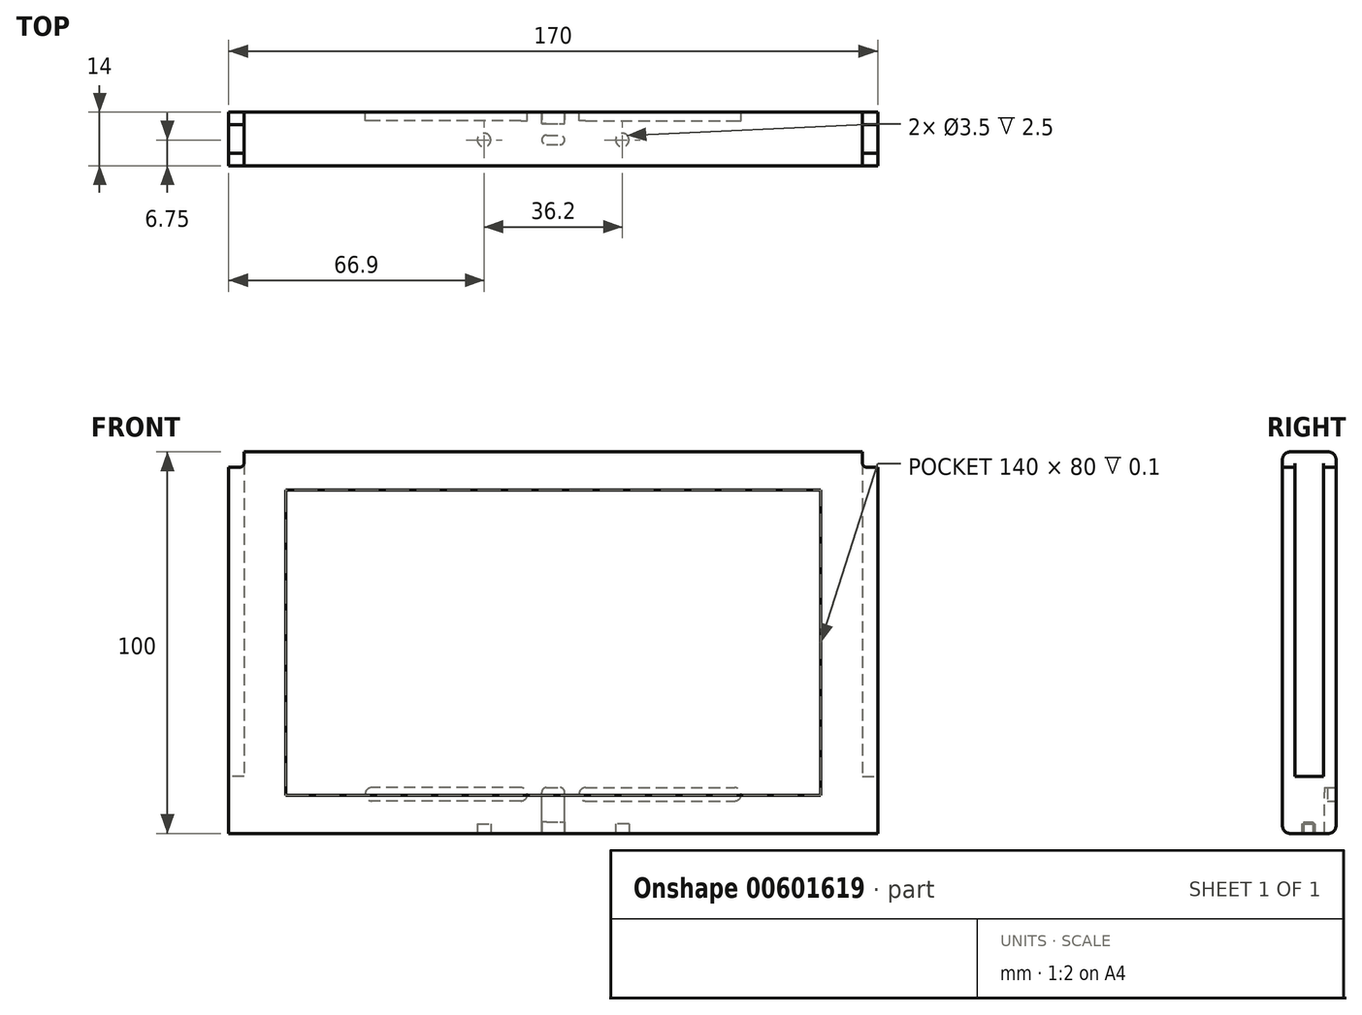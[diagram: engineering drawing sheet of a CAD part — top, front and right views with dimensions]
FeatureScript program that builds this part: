
annotation { "Feature Type Name" : "Feature", "Feature Type Description" : "" }
export const myFeature = defineFeature(function(context is Context, id is Id, definition is map)
    precondition{}
    {
        {
            var Q0;
            Q0=qCreatedBy(makeId("Front.planeOp"),FACE);
            var sketch = newSketch(context, id + "F0", { "sketchPlane" : qUnion([Q0])});
            skLineSegment(sketch, "E0.left", {"start": v(0, 0) * mm, "end": v(0, 100) * mm});
            skLineSegment(sketch, "E1", {"start": v(85, 100) * mm, "end": v(85, 0) * mm});
            skLineSegment(sketch, "E2", {"start": v(0, 0) * mm, "end": v(85, 0) * mm});
            skLineSegment(sketch, "E3", {"start": v(0, 100) * mm, "end": v(85, 100) * mm});
            skLineSegment(sketch, "E4.bottom", {"start": v(15, 90) * mm, "end": v(85, 90) * mm});
            skLineSegment(sketch, "E4.top", {"start": v(15, 10) * mm, "end": v(85, 10) * mm});
            skLineSegment(sketch, "E4.left", {"start": v(15, 90) * mm, "end": v(15, 10) * mm});
            skLineSegment(sketch, "E4.right", {"start": v(85, 90) * mm, "end": v(85, 10) * mm});
            skSolve(sketch);
        }
        {
            var Q0;
            Q0=makeQuery(id+"F0.imprint","IMPRINT",FACE,{"disambiguationData":[TD([[makeQuery(id+"F0.imprint","IMPRINT",EDGE,{"derivedFrom":sQuery(id+"F0.wireOp",EDGE,"E0.left")}),-1.0]])]});
            extrude(context, id + "F1", {"entities" : qUnion([Q0]), "depth" : 14 * mm, "offsetDistance" : 25 * mm});
        }
        {
            var Q0;
            Q0=makeQuery(id+"F1.opExtrude","CAP_EDGE",EDGE,{"disambiguationData":[OSD([sQuery(id+"F0.wireOp",EDGE,"E3")])],"isStart":false});
            var Q1;
            Q1=makeQuery(id+"F1.opExtrude","CAP_EDGE",EDGE,{"disambiguationData":[OSD([sQuery(id+"F0.wireOp",EDGE,"E3")])],"isStart":true});
            var Q2;
            Q2=makeQuery(id+"F1.opExtrude","CAP_EDGE",EDGE,{"disambiguationData":[OSD([sQuery(id+"F0.wireOp",EDGE,"E2")])],"isStart":false});
            var Q3;
            Q3=makeQuery(id+"F1.opExtrude","CAP_EDGE",EDGE,{"disambiguationData":[OSD([sQuery(id+"F0.wireOp",EDGE,"E2")])],"isStart":true});
            fillet(context, id + "F2", {"entities" : qUnion([Q0, Q1, Q2, Q3]), "radius" : 2 * mm, "allowEdgeOverflow" : false});
        }
        {
            var Q0;
            Q0=makeQuery(id+"F0.imprint","IMPRINT",FACE,{"disambiguationData":[TD([[makeQuery(id+"F0.imprint","IMPRINT",EDGE,{"derivedFrom":sQuery(id+"F0.wireOp",EDGE,"E4.bottom")}),-1.0]])]});
            extrude(context, id + "F3", {"entities" : qUnion([Q0]), "operationType" : NewBodyOperationType.ADD, "depth" : 13.9 * mm, "offsetDistance" : 25 * mm});
        }
        {
            var Q0;
            Q0=makeQuery(id+"F1.opExtrude","SWEPT_FACE",FACE,{"disambiguationData":[OSD([sQuery(id+"F0.wireOp",EDGE,"E0.left")])]});
            var sketch = newSketch(context, id + "F4", { "sketchPlane" : qUnion([Q0])});
            skLineSegment(sketch, "E5.bottom", {"start": v(3.3, 100) * mm, "end": v(10.7, 100) * mm});
            skLineSegment(sketch, "E5.top", {"start": v(3.3, 15) * mm, "end": v(10.7, 15) * mm});
            skLineSegment(sketch, "E5.left", {"start": v(3.3, 100) * mm, "end": v(3.3, 15) * mm});
            skLineSegment(sketch, "E5.right", {"start": v(10.7, 100) * mm, "end": v(10.7, 15) * mm});
            skLineSegment(sketch, "E6.bottom", {"start": v(0, 100) * mm, "end": v(14, 100) * mm});
            skLineSegment(sketch, "E6.top", {"start": v(0, 96) * mm, "end": v(14, 96) * mm});
            skLineSegment(sketch, "E6.left", {"start": v(0, 100) * mm, "end": v(0, 96) * mm});
            skLineSegment(sketch, "E6.right", {"start": v(14, 100) * mm, "end": v(14, 96) * mm});
            skSolve(sketch);
        }
        {
            var Q0;
            {var subQ2=sQuery(id+"F0.wireOp",EDGE,"E0.left");var subQ6=makeQuery(id+"F2.opFillet","BLEND_EDGE",EDGE,{"blendedFrom":[makeQuery(id+"F1.opExtrude","CAP_EDGE",EDGE,{"disambiguationData":[OSD([sQuery(id+"F0.wireOp",EDGE,"E3")])],"isStart":false}),makeQuery(id+"F1.opExtrude","SWEPT_FACE",FACE,{"disambiguationData":[OSD([subQ2])]})],"blendedInto":[makeQuery(id+"F1.opExtrude","SWEPT_FACE",FACE,{"disambiguationData":[OSD([subQ2])]})]});Q0=makeQuery(id+"F4.imprint","IMPRINT",FACE,{"disambiguationData":[TD([[makeQuery(id+"F4.imprint","IMPRINT",EDGE,{"derivedFrom":subQ6}),1.0]])]});}
            var Q1;
            {var subQ0=sQuery(id+"F4.wireOp",EDGE,"E6.bottom");var subQ1=sQuery(id+"F4.wireOp",EDGE,"E5.left");var subQ2=makeQuery(id+"F4.imprint","INTERSECT",VERTEX,{"derivedFrom":[subQ1,subQ0]});Q1=makeQuery(id+"F4.imprint","IMPRINT",FACE,{"disambiguationData":[TD([[makeQuery(id+"F4.imprint","IMPRINT",EDGE,{"disambiguationData":[TD([[subQ2,-1.0]])],"derivedFrom":subQ1}),1.0]])]});}
            var Q2;
            {var subQ2=sQuery(id+"F0.wireOp",EDGE,"E0.left");var subQ6=makeQuery(id+"F2.opFillet","BLEND_EDGE",EDGE,{"blendedFrom":[makeQuery(id+"F1.opExtrude","CAP_EDGE",EDGE,{"disambiguationData":[OSD([sQuery(id+"F0.wireOp",EDGE,"E3")])],"isStart":true}),makeQuery(id+"F1.opExtrude","SWEPT_FACE",FACE,{"disambiguationData":[OSD([subQ2])]})],"blendedInto":[makeQuery(id+"F1.opExtrude","SWEPT_FACE",FACE,{"disambiguationData":[OSD([subQ2])]})]});Q2=makeQuery(id+"F4.imprint","IMPRINT",FACE,{"disambiguationData":[TD([[makeQuery(id+"F4.imprint","IMPRINT",EDGE,{"derivedFrom":subQ6}),1.0]])]});}
            var Q3;
            {var subQ0=sQuery(id+"F4.wireOp",EDGE,"E5.top");Q3=makeQuery(id+"F4.imprint","IMPRINT",FACE,{"disambiguationData":[TD([[makeQuery(id+"F4.imprint","IMPRINT",EDGE,{"derivedFrom":subQ0}),1.0]])]});}
            extrude(context, id + "F5", {"entities" : qUnion([Q0, Q1, Q2, Q3]), "operationType" : NewBodyOperationType.REMOVE, "oppositeDirection" : true, "depth" : 4 * mm, "offsetDistance" : 25 * mm});
        }
        {
            var Q0;
            {var subQ0=sQuery(id+"F4.wireOp",EDGE,"E6.top");Q0=makeQuery(id+"F5.boolean.opBoolean","COPY",EDGE,{"derivedFrom":makeQuery(id+"F5.opExtrude","CAP_EDGE",EDGE,{"disambiguationData":[OSD([subQ0]),TDD([makeQuery(id+"F4.imprint","IMPRINT",EDGE,{"disambiguationData":[TD([[makeQuery(id+"F4.imprint","INTERSECT",VERTEX,{"derivedFrom":[sQuery(id+"F4.wireOp",EDGE,"E5.left"),subQ0]}),1.0]])],"derivedFrom":subQ0})])],"isStart":false})});}
            var Q1;
            {var subQ0=sQuery(id+"F4.wireOp",EDGE,"E6.top");Q1=makeQuery(id+"F5.boolean.opBoolean","COPY",EDGE,{"derivedFrom":makeQuery(id+"F5.opExtrude","CAP_EDGE",EDGE,{"disambiguationData":[OSD([subQ0]),TDD([makeQuery(id+"F4.imprint","IMPRINT",EDGE,{"disambiguationData":[TD([[makeQuery(id+"F4.imprint","INTERSECT",VERTEX,{"derivedFrom":[sQuery(id+"F4.wireOp",EDGE,"E5.right"),subQ0]}),-1.0]])],"derivedFrom":subQ0})])],"isStart":false})});}
            fillet(context, id + "F6", {"entities" : qUnion([Q0, Q1]), "radius" : 1 * mm, "tangentPropagation" : true, "allowEdgeOverflow" : false});
        }
        {
            var Q0;
            Q0=makeQuery(id+"F0.imprint","IMPRINT",FACE,{"disambiguationData":[TD([[makeQuery(id+"F0.imprint","IMPRINT",EDGE,{"derivedFrom":sQuery(id+"F0.wireOp",EDGE,"E4.bottom")}),-1.0]])]});
            var sketch = newSketch(context, id + "F7", { "sketchPlane" : qUnion([Q0])});
            skLineSegment(sketch, "E7.bottom", {"start": v(0, 0) * mm, "end": v(82, 0) * mm});
            skLineSegment(sketch, "E7.top", {"start": v(0, 28.87) * mm, "end": v(82, 28.87) * mm});
            skLineSegment(sketch, "E7.left", {"start": v(0, 0) * mm, "end": v(0, 28.87) * mm});
            skLineSegment(sketch, "E7.right", {"start": v(82, 0) * mm, "end": v(82, 28.87) * mm});
            skLineSegment(sketch, "E8.bottom", {"start": v(82, 0) * mm, "end": v(85, 0) * mm});
            skLineSegment(sketch, "E8.top", {"start": v(83.2, 12) * mm, "end": v(85, 12) * mm});
            skLineSegment(sketch, "E8.left", {"start": v(82, 0) * mm, "end": v(82, 10.8) * mm});
            skLineSegment(sketch, "E8.right", {"start": v(85, 0) * mm, "end": v(85, 12) * mm});
            skPoint(sketch, "E9.visualSharp", {"position": v(82, 12) * mm});
            skArc(sketch, "E9.filletArc", {"start": v(83.2, 12) * mm, "mid": v(82.35, 11.65) * mm, "end": v(82, 10.8) * mm});
            skLineSegment(sketch, "E10.bottom", {"start": v(76.5, 12) * mm, "end": v(37.5, 12) * mm});
            skLineSegment(sketch, "E10.top", {"start": v(76.5, 8.5) * mm, "end": v(37.5, 8.5) * mm});
            skLineSegment(sketch, "E10.left", {"start": v(78.25, 10.25) * mm, "end": v(78.25, 10.25) * mm});
            skLineSegment(sketch, "E10.right", {"start": v(35.75, 10.25) * mm, "end": v(35.75, 10.25) * mm});
            skPoint(sketch, "E11.visualSharp", {"position": v(78.25, 12) * mm});
            skArc(sketch, "E11.filletArc", {"start": v(78.25, 10.25) * mm, "mid": v(77.74, 11.49) * mm, "end": v(76.5, 12) * mm});
            skPoint(sketch, "E12.visualSharp", {"position": v(78.25, 8.5) * mm});
            skArc(sketch, "E12.filletArc", {"start": v(76.5, 8.5) * mm, "mid": v(77.74, 9.01) * mm, "end": v(78.25, 10.25) * mm});
            skPoint(sketch, "E13.visualSharp", {"position": v(35.75, 12) * mm});
            skArc(sketch, "E13.filletArc", {"start": v(37.5, 12) * mm, "mid": v(36.26, 11.49) * mm, "end": v(35.75, 10.25) * mm});
            skPoint(sketch, "E14.visualSharp", {"position": v(35.75, 8.5) * mm});
            skArc(sketch, "E14.filletArc", {"start": v(35.75, 10.25) * mm, "mid": v(36.26, 9.01) * mm, "end": v(37.5, 8.5) * mm});
            skSolve(sketch);
        }
        {
            var Q0;
            {var subQ3=sQuery(id+"F7.wireOp",EDGE,"E8.top");Q0=makeQuery(id+"F7.imprint","IMPRINT",FACE,{"disambiguationData":[TD([[makeQuery(id+"F7.imprint","IMPRINT",EDGE,{"derivedFrom":subQ3}),-1.0]])]});}
            var Q1;
            {var subQ0=sQuery(id+"F7.wireOp",EDGE,"E8.bottom");Q1=makeQuery(id+"F7.imprint","IMPRINT",FACE,{"disambiguationData":[TD([[makeQuery(id+"F7.imprint","IMPRINT",EDGE,{"derivedFrom":subQ0}),1.0]])]});}
            extrude(context, id + "F8", {"entities" : qUnion([Q0, Q1]), "operationType" : NewBodyOperationType.REMOVE, "depth" : 3 * mm, "offsetDistance" : 25 * mm});
        }
        {
            var Q0;
            Q0=makeQuery(id+"F7.imprint","IMPRINT",FACE,{"disambiguationData":[TD([[makeQuery(id+"F7.imprint","IMPRINT",EDGE,{"derivedFrom":sQuery(id+"F7.wireOp",EDGE,"E10.bottom")}),1.0]])]});
            var Q1;
            {var subQ0=sQuery(id+"F7.wireOp",EDGE,"E10.top");Q1=makeQuery(id+"F7.imprint","IMPRINT",FACE,{"disambiguationData":[TD([[makeQuery(id+"F7.imprint","IMPRINT",EDGE,{"derivedFrom":subQ0}),-1.0]])]});}
            extrude(context, id + "F9", {"entities" : qUnion([Q0, Q1]), "operationType" : NewBodyOperationType.REMOVE, "depth" : 2.25 * mm, "offsetDistance" : 25 * mm});
        }
        {
            var Q0;
            {var subQ0=makeQuery(id+"F1.opExtrude","SWEPT_FACE",FACE,{"disambiguationData":[OSD([sQuery(id+"F0.wireOp",EDGE,"E2")])]});Q0=makeQuery(id+"F13.boolean.opBoolean","MERGE",FACE,{"derivedFrom":[subQ0,makeQuery(id+"F13.opPattern","COPY",FACE,{"derivedFrom":subQ0,"instanceName":"1"})]});}
            var sketch = newSketch(context, id + "F10", { "sketchPlane" : qUnion([Q0])});
            skLineSegment(sketch, "E15", {"start": v(85, 0) * mm, "end": v(85, 14) * mm});
            skPoint(sketch, "E15.endSnap0", {"position": v(85, 3.08) * mm});
            skLineSegment(sketch, "E16.bottom", {"start": v(83.25, 6) * mm, "end": v(85, 6) * mm});
            skLineSegment(sketch, "E16.top", {"start": v(83.25, 8.5) * mm, "end": v(85, 8.5) * mm});
            skLineSegment(sketch, "E16.left", {"start": v(82, 7.25) * mm, "end": v(82, 7.25) * mm});
            skLineSegment(sketch, "E16.right", {"start": v(85, 6) * mm, "end": v(85, 8.5) * mm});
            skPoint(sketch, "E17.visualSharp", {"position": v(82, 6) * mm});
            skArc(sketch, "E17.filletArc", {"start": v(82, 7.25) * mm, "mid": v(82.37, 6.37) * mm, "end": v(83.25, 6) * mm});
            skPoint(sketch, "E18.visualSharp", {"position": v(82, 8.5) * mm});
            skArc(sketch, "E18.filletArc", {"start": v(83.25, 8.5) * mm, "mid": v(82.37, 8.13) * mm, "end": v(82, 7.25) * mm});
            skCircle(sketch, "E19", {"center": v(66.9, 7.25) * mm, "radius": 1.75 * mm});
            skSolve(sketch);
        }
        {
            var Q0;
            Q0=makeQuery(id+"F10.imprint","IMPRINT",FACE,{"disambiguationData":[TD([[makeQuery(id+"F10.imprint","IMPRINT",EDGE,{"derivedFrom":sQuery(id+"F10.wireOp",EDGE,"E16.bottom")}),1.0]])]});
            extrude(context, id + "F11", {"entities" : qUnion([Q0]), "operationType" : NewBodyOperationType.REMOVE, "oppositeDirection" : true, "depth" : 3 * mm, "offsetDistance" : 25 * mm});
        }
        {
            var Q0;
            Q0=makeQuery(id+"F10.imprint","IMPRINT",FACE,{"disambiguationData":[TD([[makeQuery(id+"F10.imprint","IMPRINT",EDGE,{"derivedFrom":sQuery(id+"F10.wireOp",EDGE,"E19")}),1.0]])]});
            extrude(context, id + "F12", {"entities" : qUnion([Q0]), "operationType" : NewBodyOperationType.REMOVE, "oppositeDirection" : true, "depth" : 2.5 * mm, "offsetDistance" : 25 * mm});
        }
        {
            var Q0;
            Q0=makeQuery(id+"F1.opExtrude","SWEPT_BODY",BODY,{"disambiguationData":[OSD([sQuery(id+"F0.wireOp",EDGE,"E0.left"),sQuery(id+"F0.wireOp",EDGE,"E1"),sQuery(id+"F0.wireOp",EDGE,"E2"),sQuery(id+"F0.wireOp",EDGE,"E3")])]});
            var Q1;
            Q1=makeQuery(id+"F1.opExtrude","SWEPT_FACE",FACE,{"disambiguationData":[OSD([sQuery(id+"F0.wireOp",EDGE,"E1")])]});
            mirror(context, id + "F13", {"operationType" : NewBodyOperationType.ADD, "entities" : qUnion([Q0]), "mirrorPlane" : qUnion([Q1])});
        }
    });
